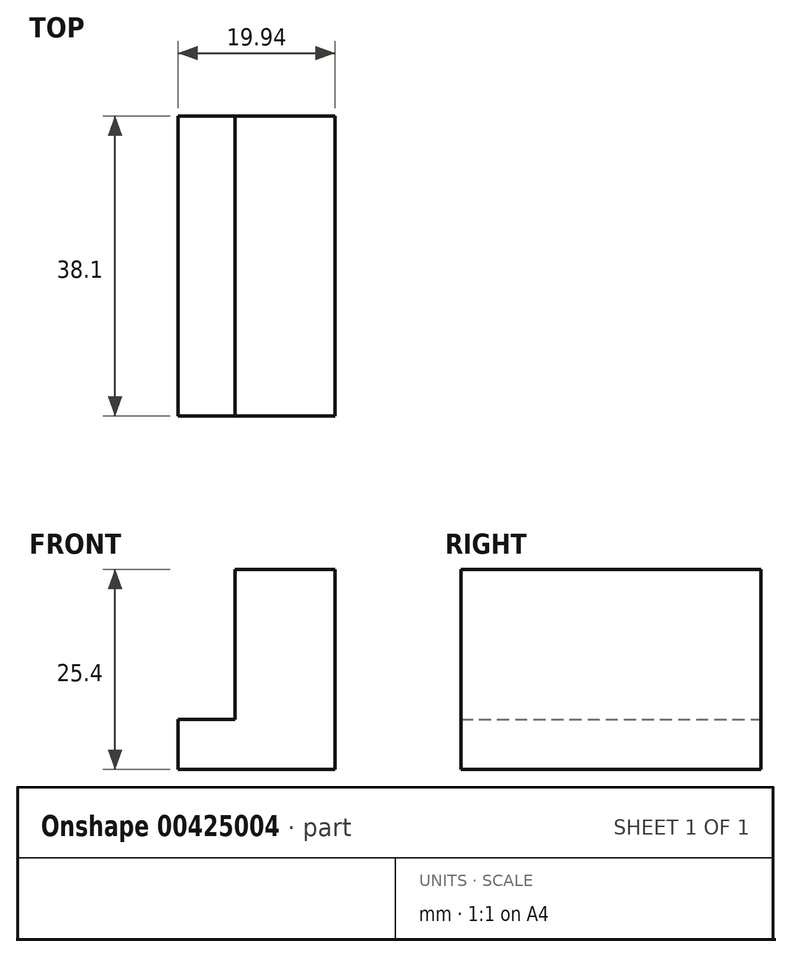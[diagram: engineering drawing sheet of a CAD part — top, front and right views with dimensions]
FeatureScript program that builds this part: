
annotation { "Feature Type Name" : "Feature", "Feature Type Description" : "" }
export const myFeature = defineFeature(function(context is Context, id is Id, definition is map)
    precondition{}
    {
        {
            var Q0;
            Q0=qCreatedBy(makeId("Front.planeOp"),FACE);
            var sketch = newSketch(context, id + "F0", { "sketchPlane" : qUnion([Q0])});
            skLineSegment(sketch, "E0", {"start": v(0, 0) * mm, "end": v(0, 6.35) * mm});
            skLineSegment(sketch, "E1", {"start": v(0, 6.35) * mm, "end": v(7.24, 6.35) * mm});
            skLineSegment(sketch, "E2", {"start": v(7.24, 6.35) * mm, "end": v(7.24, 25.4) * mm});
            skLineSegment(sketch, "E3", {"start": v(7.24, 25.4) * mm, "end": v(19.94, 25.4) * mm});
            skLineSegment(sketch, "E4", {"start": v(19.94, 25.4) * mm, "end": v(19.94, 0) * mm});
            skLineSegment(sketch, "E5", {"start": v(0, 0) * mm, "end": v(19.94, 0) * mm});
            skSolve(sketch);
        }
        {
            var Q0;
            Q0 = qSketchRegion(id + "F0", true);
            extrude(context, id + "F1", {"entities" : qUnion([Q0]), "depth" : 38.1 * mm});
        }
    });
